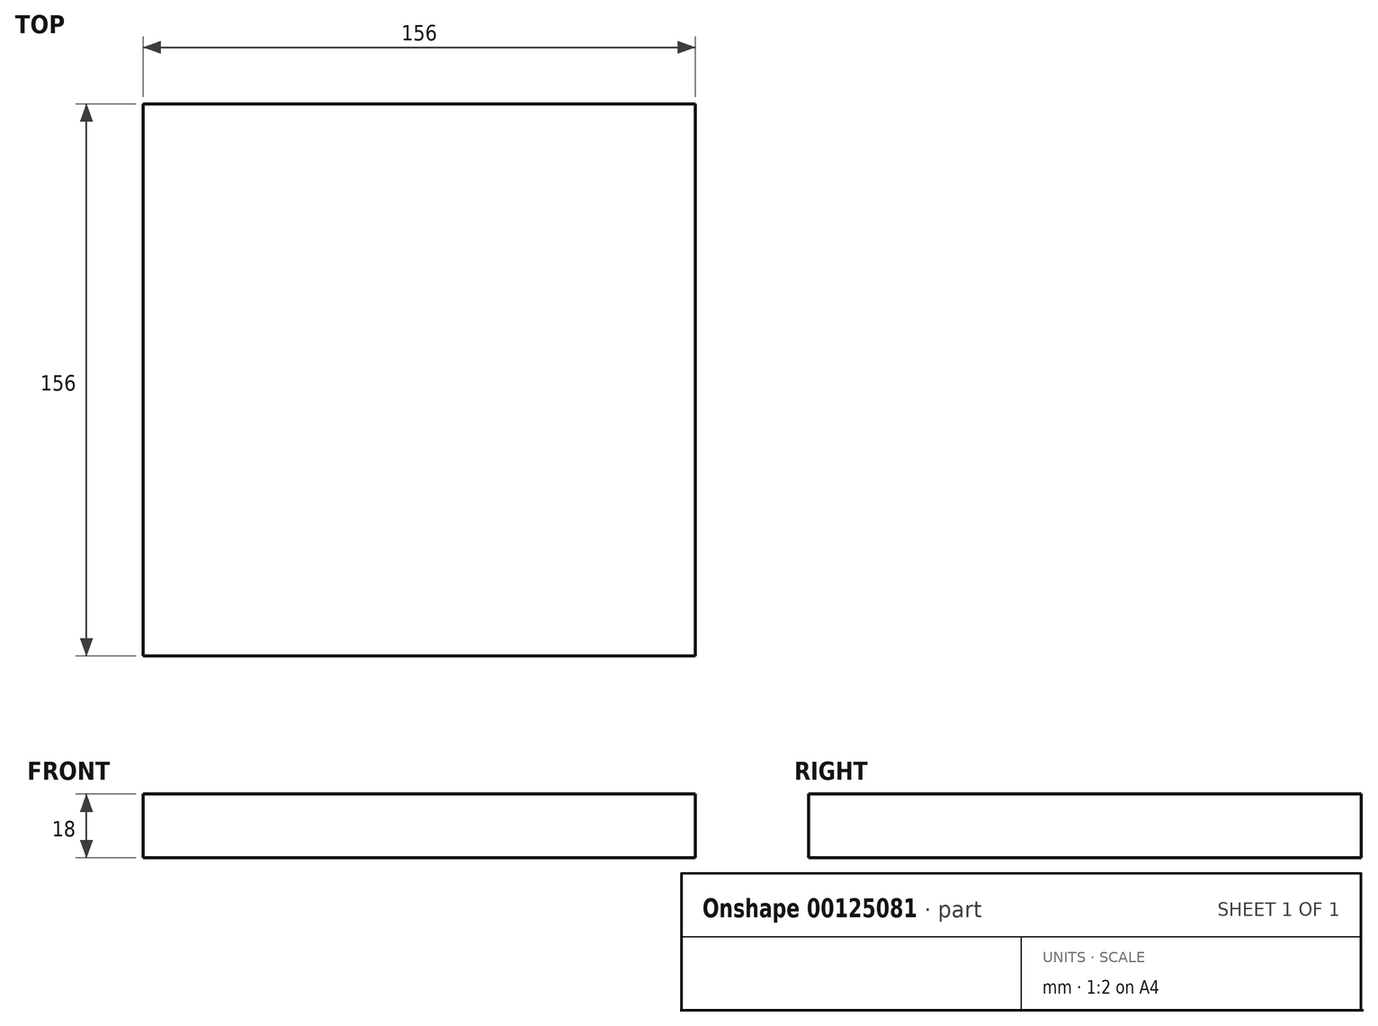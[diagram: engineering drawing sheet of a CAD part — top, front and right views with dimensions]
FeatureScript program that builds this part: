
annotation { "Feature Type Name" : "Feature", "Feature Type Description" : "" }
export const myFeature = defineFeature(function(context is Context, id is Id, definition is map)
    precondition{}
    {
        {
            var Q0;
            Q0=qCreatedBy(makeId("Top.planeOp"),FACE);
            var sketch = newSketch(context, id + "F0", { "sketchPlane" : qUnion([Q0])});
            skLineSegment(sketch, "E0.bottom", {"start": v(78, -78) * mm, "end": v(-78, -78) * mm});
            skLineSegment(sketch, "E0.top", {"start": v(78, 78) * mm, "end": v(-78, 78) * mm});
            skLineSegment(sketch, "E0.left", {"start": v(78, -78) * mm, "end": v(78, 78) * mm});
            skLineSegment(sketch, "E0.right", {"start": v(-78, -78) * mm, "end": v(-78, 78) * mm});
            skPoint(sketch, "E0.middle", {"position": v(0, 0) * mm});
            skSolve(sketch);
        }
        {
            var Q0;
            Q0 = qSketchRegion(id + "F0", true);
            extrude(context, id + "F1", {"entities" : qUnion([Q0]), "depth" : 18 * mm});
        }
    });
